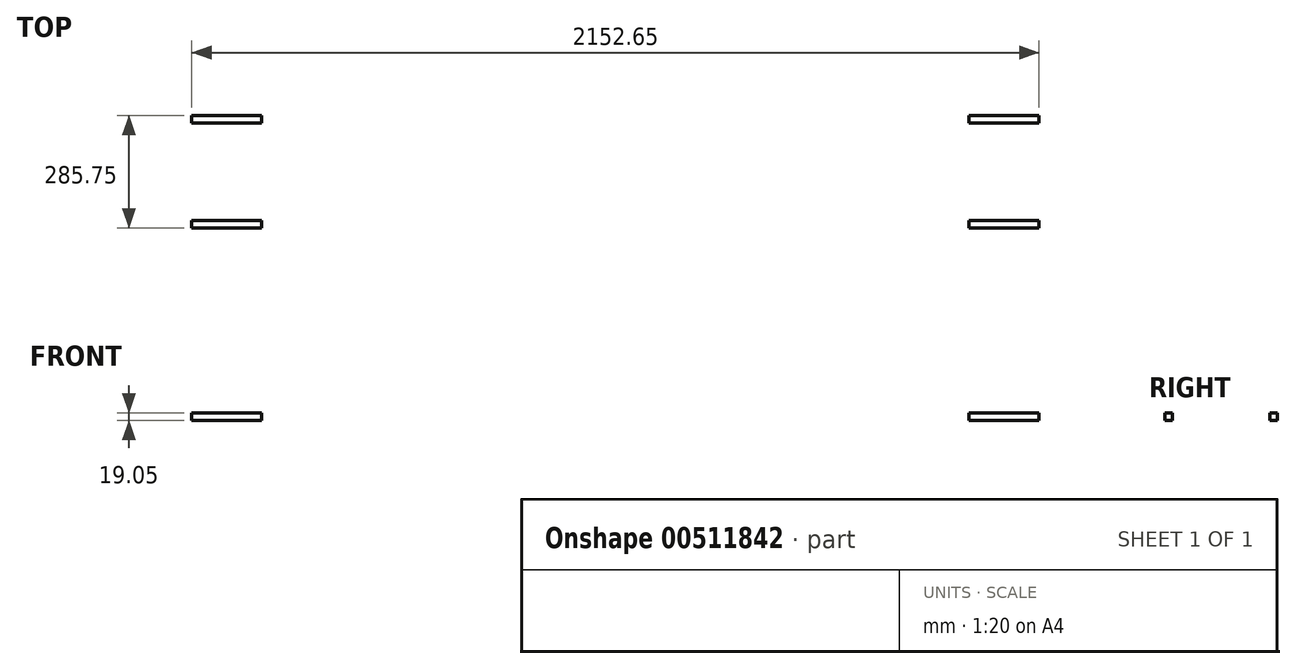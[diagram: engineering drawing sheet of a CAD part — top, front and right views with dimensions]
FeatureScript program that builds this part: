
annotation { "Feature Type Name" : "Feature", "Feature Type Description" : "" }
export const myFeature = defineFeature(function(context is Context, id is Id, definition is map)
    precondition{}
    {
        {
            var Q0;
            Q0=qCreatedBy(makeId("Top.planeOp"),FACE);
            var sketch = newSketch(context, id + "F0", { "sketchPlane" : qUnion([Q0])});
            skLineSegment(sketch, "E0.bottom", {"start": v(-1271.07, 126.53) * mm, "end": v(1148.28, 126.53) * mm});
            skLineSegment(sketch, "E0.top", {"start": v(-1271.07, -159.22) * mm, "end": v(1148.28, -159.22) * mm});
            skLineSegment(sketch, "E0.left", {"start": v(-1271.07, 126.53) * mm, "end": v(-1271.07, -159.22) * mm});
            skLineSegment(sketch, "E0.right", {"start": v(1148.28, 126.53) * mm, "end": v(1148.28, -159.22) * mm});
            skLineSegment(sketch, "E1", {"start": v(-1271.07, -16.35) * mm, "end": v(1148.28, -16.35) * mm, "construction": true});
            skLineSegment(sketch, "E2", {"start": v(-61.4, 126.53) * mm, "end": v(-61.4, -159.22) * mm, "construction": true});
            skLineSegment(sketch, "E3", {"start": v(-1137.72, -159.22) * mm, "end": v(-1137.72, -140.17) * mm});
            skLineSegment(sketch, "E4", {"start": v(-1137.72, -140.17) * mm, "end": v(-959.92, -140.17) * mm});
            skLineSegment(sketch, "E5", {"start": v(-959.92, -140.17) * mm, "end": v(-959.92, -159.22) * mm});
            skLineSegment(sketch, "E6.MirrorCS", {"start": v(-1137.72, 107.48) * mm, "end": v(-959.92, 107.48) * mm});
            skLineSegment(sketch, "E7.MirrorCS", {"start": v(-1137.72, 126.53) * mm, "end": v(-1137.72, 107.48) * mm});
            skLineSegment(sketch, "E8.MirrorCS", {"start": v(-959.92, 107.48) * mm, "end": v(-959.92, 126.53) * mm});
            skLineSegment(sketch, "E9.MirrorCS", {"start": v(1014.93, 126.53) * mm, "end": v(1014.93, 107.48) * mm});
            skLineSegment(sketch, "E10.MirrorCS", {"start": v(837.13, 107.48) * mm, "end": v(837.13, 126.53) * mm});
            skLineSegment(sketch, "E11.MirrorCS", {"start": v(1014.93, 107.48) * mm, "end": v(837.13, 107.48) * mm});
            skLineSegment(sketch, "E12.MirrorCS", {"start": v(1148.28, 126.53) * mm, "end": v(-1271.07, 126.53) * mm});
            skLineSegment(sketch, "E13.MirrorCS", {"start": v(1014.93, -159.22) * mm, "end": v(1014.93, -140.17) * mm});
            skLineSegment(sketch, "E14.MirrorCS", {"start": v(1014.93, -140.17) * mm, "end": v(837.13, -140.17) * mm});
            skLineSegment(sketch, "E15.MirrorCS", {"start": v(837.13, -140.17) * mm, "end": v(837.13, -159.22) * mm});
            skLineSegment(sketch, "E16.bottom", {"start": v(-928.17, 126.53) * mm, "end": v(-318.57, 126.53) * mm});
            skLineSegment(sketch, "E16.top", {"start": v(-928.17, -159.22) * mm, "end": v(-318.57, -159.22) * mm});
            skLineSegment(sketch, "E16.left", {"start": v(-928.17, 37.63) * mm, "end": v(-928.17, -70.32) * mm});
            skLineSegment(sketch, "E16.right", {"start": v(-318.57, 37.63) * mm, "end": v(-318.57, -70.32) * mm});
            skLineSegment(sketch, "E17", {"start": v(-877.37, 88.43) * mm, "end": v(-369.37, 88.43) * mm});
            skLineSegment(sketch, "E18", {"start": v(-318.57, 88.43) * mm, "end": v(-318.57, -121.12) * mm});
            skLineSegment(sketch, "E19", {"start": v(-369.37, -121.12) * mm, "end": v(-877.37, -121.12) * mm});
            skLineSegment(sketch, "E20.MirrorCS", {"start": v(246.58, -121.12) * mm, "end": v(754.58, -121.12) * mm});
            skLineSegment(sketch, "E21.MirrorCS", {"start": v(195.78, 37.63) * mm, "end": v(195.78, -70.32) * mm});
            skLineSegment(sketch, "E22.MirrorCS", {"start": v(754.58, 88.43) * mm, "end": v(246.58, 88.43) * mm});
            skLineSegment(sketch, "E23.MirrorCS", {"start": v(805.38, 37.63) * mm, "end": v(805.38, -70.32) * mm});
            skPoint(sketch, "E24.newPointA", {"position": v(-928.17, -159.22) * mm});
            skPoint(sketch, "E24.newPointB", {"position": v(-928.17, -121.12) * mm});
            skArc(sketch, "E24.filletArc", {"start": v(-928.17, -70.32) * mm, "mid": v(-913.3, -106.24) * mm, "end": v(-877.37, -121.12) * mm});
            skPoint(sketch, "E25.newPointA", {"position": v(-928.17, 126.53) * mm});
            skPoint(sketch, "E25.newPointB", {"position": v(-928.17, 88.43) * mm});
            skArc(sketch, "E25.filletArc", {"start": v(-877.37, 88.43) * mm, "mid": v(-913.3, 73.55) * mm, "end": v(-928.17, 37.63) * mm});
            skPoint(sketch, "E26.newPointA", {"position": v(-318.57, -121.12) * mm});
            skPoint(sketch, "E26.newPointB", {"position": v(-318.57, -159.22) * mm});
            skArc(sketch, "E26.filletArc", {"start": v(-369.37, -121.12) * mm, "mid": v(-333.45, -106.24) * mm, "end": v(-318.57, -70.32) * mm});
            skPoint(sketch, "E27.newPointA", {"position": v(-318.57, 88.43) * mm});
            skPoint(sketch, "E27.newPointB", {"position": v(-318.57, 126.53) * mm});
            skArc(sketch, "E27.filletArc", {"start": v(-318.57, 37.63) * mm, "mid": v(-333.45, 73.55) * mm, "end": v(-369.37, 88.43) * mm});
            skPoint(sketch, "E28.newPointA", {"position": v(195.78, -159.22) * mm});
            skPoint(sketch, "E28.newPointB", {"position": v(195.78, -121.12) * mm});
            skArc(sketch, "E28.filletArc", {"start": v(195.78, -70.32) * mm, "mid": v(210.66, -106.24) * mm, "end": v(246.58, -121.12) * mm});
            skPoint(sketch, "E29.newPointA", {"position": v(195.78, 126.53) * mm});
            skPoint(sketch, "E29.newPointB", {"position": v(195.78, 88.43) * mm});
            skArc(sketch, "E29.filletArc", {"start": v(246.58, 88.43) * mm, "mid": v(210.66, 73.55) * mm, "end": v(195.78, 37.63) * mm});
            skPoint(sketch, "E30.newPointA", {"position": v(805.38, 88.43) * mm});
            skPoint(sketch, "E30.newPointB", {"position": v(805.38, 126.53) * mm});
            skArc(sketch, "E30.filletArc", {"start": v(805.38, 37.63) * mm, "mid": v(790.5, 73.55) * mm, "end": v(754.58, 88.43) * mm});
            skPoint(sketch, "E31.newPointA", {"position": v(805.38, -159.22) * mm});
            skPoint(sketch, "E31.newPointB", {"position": v(805.38, -121.12) * mm});
            skArc(sketch, "E31.filletArc", {"start": v(754.58, -121.12) * mm, "mid": v(790.5, -106.24) * mm, "end": v(805.38, -70.32) * mm});
            skLineSegment(sketch, "E32.bottom", {"start": v(-204.27, -121.12) * mm, "end": v(81.48, -121.12) * mm});
            skLineSegment(sketch, "E32.top", {"start": v(-204.27, 88.43) * mm, "end": v(81.48, 88.43) * mm});
            skLineSegment(sketch, "E32.left", {"start": v(-255.07, -70.32) * mm, "end": v(-255.07, 37.63) * mm});
            skLineSegment(sketch, "E32.right", {"start": v(132.28, -70.32) * mm, "end": v(132.28, 37.63) * mm});
            skPoint(sketch, "E33.visualSharp", {"position": v(-255.07, -121.12) * mm});
            skArc(sketch, "E33.filletArc", {"start": v(-255.07, -70.32) * mm, "mid": v(-240.2, -106.24) * mm, "end": v(-204.27, -121.12) * mm});
            skPoint(sketch, "E34.visualSharp", {"position": v(-255.07, 88.43) * mm});
            skArc(sketch, "E34.filletArc", {"start": v(-204.27, 88.43) * mm, "mid": v(-240.2, 73.55) * mm, "end": v(-255.07, 37.63) * mm});
            skPoint(sketch, "E35.visualSharp", {"position": v(132.28, 88.43) * mm});
            skArc(sketch, "E35.filletArc", {"start": v(132.28, 37.63) * mm, "mid": v(117.4, 73.55) * mm, "end": v(81.48, 88.43) * mm});
            skPoint(sketch, "E36.visualSharp", {"position": v(132.28, -121.12) * mm});
            skArc(sketch, "E36.filletArc", {"start": v(81.48, -121.12) * mm, "mid": v(117.4, -106.24) * mm, "end": v(132.28, -70.32) * mm});
            skSolve(sketch);
        }
        {
            var Q0;
            {var subQ8=sQuery(id+"F0.wireOp",EDGE,"E0.left");Q0=makeQuery(id+"F0.imprint","IMPRINT",FACE,{"disambiguationData":[TD([[makeQuery(id+"F0.imprint","IMPRINT",EDGE,{"derivedFrom":subQ8}),1.0]])]});}
            var Q1;
            Q1=makeQuery(id+"F0.imprint","IMPRINT",FACE,{"disambiguationData":[TD([[makeQuery(id+"F0.imprint","IMPRINT",EDGE,{"derivedFrom":sQuery(id+"F0.wireOp",EDGE,"E6.MirrorCS")}),1.0]])]});
            var Q2;
            {var subQ0=sQuery(id+"F0.wireOp",EDGE,"E3");Q2=makeQuery(id+"F0.imprint","IMPRINT",FACE,{"disambiguationData":[TD([[makeQuery(id+"F0.imprint","IMPRINT",EDGE,{"derivedFrom":subQ0}),-1.0]])]});}
            var Q3;
            Q3=makeQuery(id+"F0.imprint","IMPRINT",FACE,{"disambiguationData":[TD([[makeQuery(id+"F0.imprint","IMPRINT",EDGE,{"derivedFrom":sQuery(id+"F0.wireOp",EDGE,"E11.MirrorCS")}),-1.0]])]});
            var Q4;
            {var subQ0=sQuery(id+"F0.wireOp",EDGE,"E13.MirrorCS");Q4=makeQuery(id+"F0.imprint","IMPRINT",FACE,{"disambiguationData":[TD([[makeQuery(id+"F0.imprint","IMPRINT",EDGE,{"derivedFrom":subQ0}),1.0]])]});}
            extrude(context, id + "F1", {"entities" : qUnion([Q0, Q1, Q2, Q3, Q4]), "depth" : 19.05 * mm, "offsetDistance" : 25.4 * mm});
        }
    });
